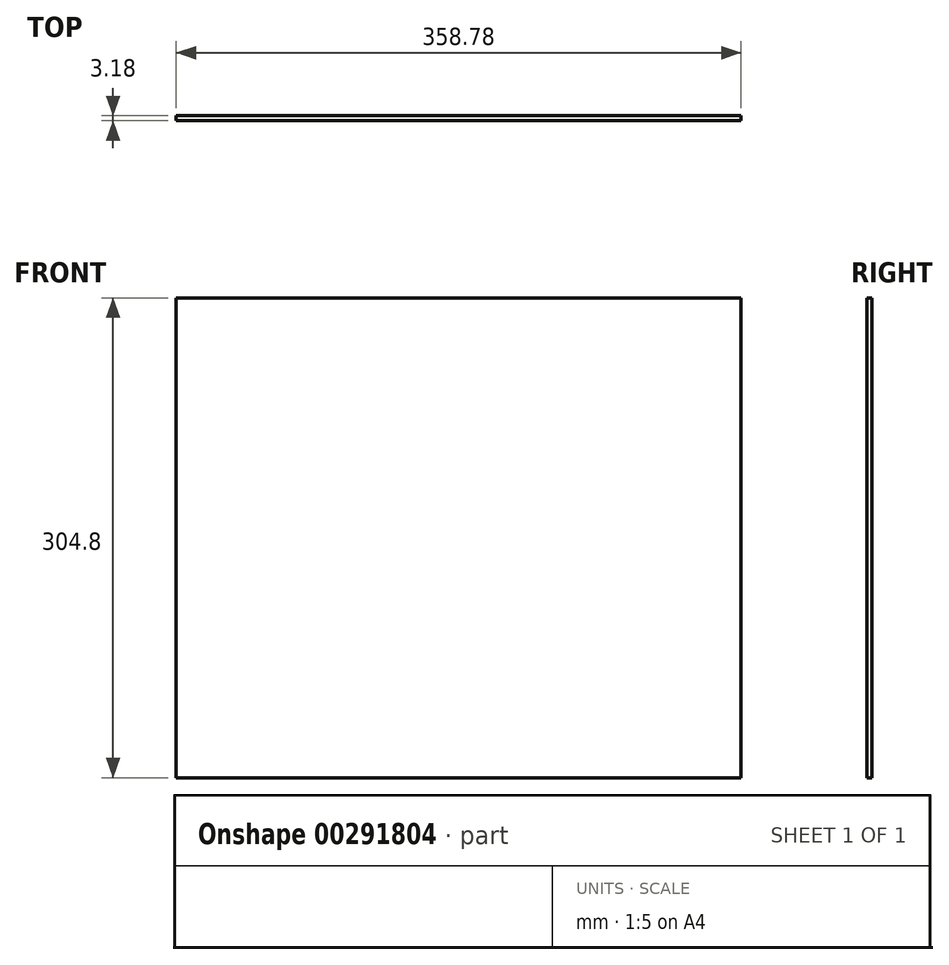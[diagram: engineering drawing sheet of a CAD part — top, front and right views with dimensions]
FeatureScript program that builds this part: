
annotation { "Feature Type Name" : "Feature", "Feature Type Description" : "" }
export const myFeature = defineFeature(function(context is Context, id is Id, definition is map)
    precondition{}
    {
        {
            var Q0;
            Q0=qCreatedBy(makeId("Front.planeOp"),FACE);
            var sketch = newSketch(context, id + "F0", { "sketchPlane" : qUnion([Q0])});
            skLineSegment(sketch, "E0.bottom", {"start": v(179.39, 152.4) * mm, "end": v(-179.39, 152.4) * mm});
            skLineSegment(sketch, "E0.top", {"start": v(179.39, -152.4) * mm, "end": v(-179.39, -152.4) * mm});
            skLineSegment(sketch, "E0.left", {"start": v(179.39, 152.4) * mm, "end": v(179.39, -152.4) * mm});
            skLineSegment(sketch, "E0.right", {"start": v(-179.39, 152.4) * mm, "end": v(-179.39, -152.4) * mm});
            skPoint(sketch, "E0.middle", {"position": v(0, 0) * mm});
            skSolve(sketch);
        }
        {
            var Q0;
            Q0 = qSketchRegion(id + "F0", true);
            extrude(context, id + "F1", {"entities" : qUnion([Q0]), "endBound" : BoundingType.SYMMETRIC, "depth" : 3.17 * mm});
        }
    });
